# Revit family: Hager-Orion_Plus-IP65-D200-Cl.I-Steel_encl-630A-UK-en
name_source: partatom
category: Equipement électrique
units: mm (PartAtom-declared; Revit-internal decimal feet)

## family parameters
Configuration du panneau = Deux colonnes, circuits au sein
Cote de connecteur circulaire = Utiliser le diamètre
Couper avec des vides une fois chargée = Non
Hôte = Face
Partagée = Non
Point de calcul de pièce = Non
Type d'élément = Tableau de raccordement

## types (14) — shared parameters
Commentaires du type = Orion Plus
EF000003 - Mounting method = EV000384 - Surface mounted (plaster)
EF000007 - Colour = EV000270 - Grey
EF000049 - Depth = 200 mm  [stored 0.656168 ft]
EF000116 - RAL-number = 7035
EF000118 - With mounting plate = Non
EF001596 - Material housing = EV000179 - Steel
EF001613 - Circuit integrity = EV000494 - None
EF004293 - Impact strength = EV008784 - IK10
EF004464 - Type of door = EV002646 - Single
EF005474 - Degree of protection (IP) = EV006421 - IP65
EF006306 - With lock = Oui
EF007800 - Suitable for lightning protection = Non
EF008873 - Nominal current (In) = 630 A
EF015940 - Cover with overpressure release = Non
Fabricant = Hager
HG000002 - With door or cover = Oui
HG000003 - Range = Orion Plus
HG000006 - Flush mounted = Non
HG000009 - Double swing door = Non
HG000010 - Asymmetric doors = Non
HG000023 - Double section enclosure = Non
HG000024 - Bottom section height = 800 mm  [stored 2.62467 ft]
HG000026 - Floor standing = Non
zero-valued in all types: EF000218 - Built-in depth, Elévation par défaut, HG000027 - Plinth height

## per-type parameters (varying)
| type | EF000008 - Width | EF000040 - Height | EF000266 - Number of rows | EF000339 - Type of cover | EF000437 - Number of conduit inlets | EF001088 - Extension possible | EF001131 - Internal depth | EF002950 - Width in number of modular spacings | EF003532 - Suitable for outdoor use | EF004427 - Number of modules | EF006244 - Transparent cover/door | EF009170 - Material plate thickness cabinet | EF009171 - Material plate thickness door/cover | EF009212 - Cover model | EF009554 - Number of openings for flange plates | HG000004 - Manufacturer reference |
| Surface mounted (plaster) IP65 W300 H350 D200  - FL105A | 300 mm | 350 mm  [stored 1.14829 ft] | 2 | EV001012 - Cover | 2 | Oui | 200 mm  [stored 0.656168 ft] | 10 | Non | 20 | Non | 2 mm  [stored 0.00656168 ft] | 2 mm  [stored 0.00656168 ft] | EV000116 - Closed | 2 | FL105A |
| Surface mounted (plaster) IP65 W300 H350 D200  - FL155A | 300 mm | 350 mm  [stored 1.14829 ft] | 2 | EV004216 - Door | 2 | Oui | 200 mm  [stored 0.656168 ft] | 10 | Non | 20 | Oui | 1 mm  [stored 0.00328084 ft] | 2 mm  [stored 0.00656168 ft] | EV000116 - Closed | 2 | FL155A |
| Surface mounted (plaster) IP65 W300 H400 D200  - FL107A | 300 mm | 400 mm  [stored 1.31234 ft] | 0 | EV004216 - Door | 2 | Non | 200 mm  [stored 0.656168 ft] | 0 | Non | 0 | Non | 2 mm  [stored 0.00656168 ft] | 2 mm  [stored 0.00656168 ft] | EV009916 - With notch | 2 | FL107A |
| Surface mounted (plaster) IP65 W300 H500 D200  - FL110A | 300 mm | 500 mm  [stored 1.64042 ft] | 3 | EV004216 - Door | 2 | Oui | 195 mm  [stored 0.639764 ft] | 10 | Non | 30 | Non | 2 mm  [stored 0.00656168 ft] | 2 mm  [stored 0.00656168 ft] | EV000116 - Closed | 2 | FL110A |
| Surface mounted (plaster) IP65 W300 H500 D200  - FL160A | 300 mm | 500 mm  [stored 1.64042 ft] | 3 | EV004216 - Door | 2 | Oui | 195 mm  [stored 0.639764 ft] | 10 | Oui | 30 | Oui | 1 mm  [stored 0.00328084 ft] | 2 mm  [stored 0.00656168 ft] | EV000116 - Closed | 2 | FL160A |
| Surface mounted (plaster) IP65 W400 H400 D200  - FL108A | 400 mm  [stored 1.31234 ft] | 400 mm  [stored 1.31234 ft] | 0 | EV004216 - Door | 2 | Non | 200 mm  [stored 0.656168 ft] | 0 | Non | 0 | Non | 2 mm  [stored 0.00656168 ft] | 2 mm  [stored 0.00656168 ft] | EV009916 - With notch | 2 | FL108A |
| Surface mounted (plaster) IP65 W400 H500 D200  - FL112A | 400 mm  [stored 1.31234 ft] | 500 mm  [stored 1.64042 ft] | 3 | EV001012 - Cover | 2 | Non | 200 mm  [stored 0.656168 ft] | 16 | Non | 48 | Non | 2 mm  [stored 0.00656168 ft] | 2 mm  [stored 0.00656168 ft] | EV000116 - Closed | 2 | FL112A |
| Surface mounted (plaster) IP65 W400 H500 D200  - FL162A | 400 mm  [stored 1.31234 ft] | 500 mm  [stored 1.64042 ft] | 3 | EV004216 - Door | 2 | Oui | 100 mm  [stored 0.328084 ft] | 16 | Non | 48 | Oui | 1 mm  [stored 0.00328084 ft] | 1 mm  [stored 0.00328084 ft] | EV000116 - Closed | 2 | FL162A |
| Surface mounted (plaster) IP65 W400 H600 D200  - FL114A | 400 mm  [stored 1.31234 ft] | 600 mm | 0 | EV004216 - Door | 2 | Non | 200 mm  [stored 0.656168 ft] | 0 | Non | 0 | Non | 2 mm  [stored 0.00656168 ft] | 2 mm  [stored 0.00656168 ft] | EV009916 - With notch | 2 | FL114A |
| Surface mounted (plaster) IP65 W400 H650 D200  - FL117A | 400 mm  [stored 1.31234 ft] | 650 mm  [stored 2.13255 ft] | 4 | EV001012 - Cover | 2 | Oui | 200 mm  [stored 0.656168 ft] | 16 | Non | 64 | Non | 2 mm  [stored 0.00656168 ft] | 2 mm  [stored 0.00656168 ft] | EV000116 - Closed | 2 | FL117A |
| Surface mounted (plaster) IP65 W400 H650 D200  - FL167A | 400 mm  [stored 1.31234 ft] | 650 mm  [stored 2.13255 ft] | 4 | EV004216 - Door | 2 | Oui | 200 mm  [stored 0.656168 ft] | 16 | Oui | 64 | Oui | 1 mm  [stored 0.00328084 ft] | 2 mm  [stored 0.00656168 ft] | EV000116 - Closed | 2 | FL167A |
| Surface mounted (plaster) IP65 W500 H500 D200  - FL113A | 500 mm  [stored 1.64042 ft] | 500 mm  [stored 1.64042 ft] | 0 | EV004216 - Door | 0 | Oui | 200 mm  [stored 0.656168 ft] | 24 | Non | 0 | Non | 2 mm  [stored 0.00656168 ft] | 2 mm  [stored 0.00656168 ft] | EV009916 - With notch | 0 | FL113A |
| Surface mounted (plaster) IP65 W500 H650 D200  - FL119A | 500 mm  [stored 1.64042 ft] | 650 mm  [stored 2.13255 ft] | 4 | EV001012 - Cover | 2 | Oui | 200 mm  [stored 0.656168 ft] | 22 | Non | 96 | Non | 2 mm  [stored 0.00656168 ft] | 2 mm  [stored 0.00656168 ft] | EV000116 - Closed | 2 | FL119A |
| Surface mounted (plaster) IP65 W500 H800 D200  - FL121A | 500 mm  [stored 1.64042 ft] | 800 mm  [stored 2.62467 ft] | 5 | EV004216 - Door | 2 | Oui | 200 mm  [stored 0.656168 ft] | 22 | Non | 110 | Non | 1 mm  [stored 0.00328084 ft] | 2 mm  [stored 0.00656168 ft] | EV000116 - Closed | 2 | FL121A |

note: [stored X ft] marks values corroborated as IEEE doubles in the binary element streams (Revit-internal decimal feet)

## geometry (parser evidence)
native form markers: Sweep x9
no freeform markers — native parametric forms only
